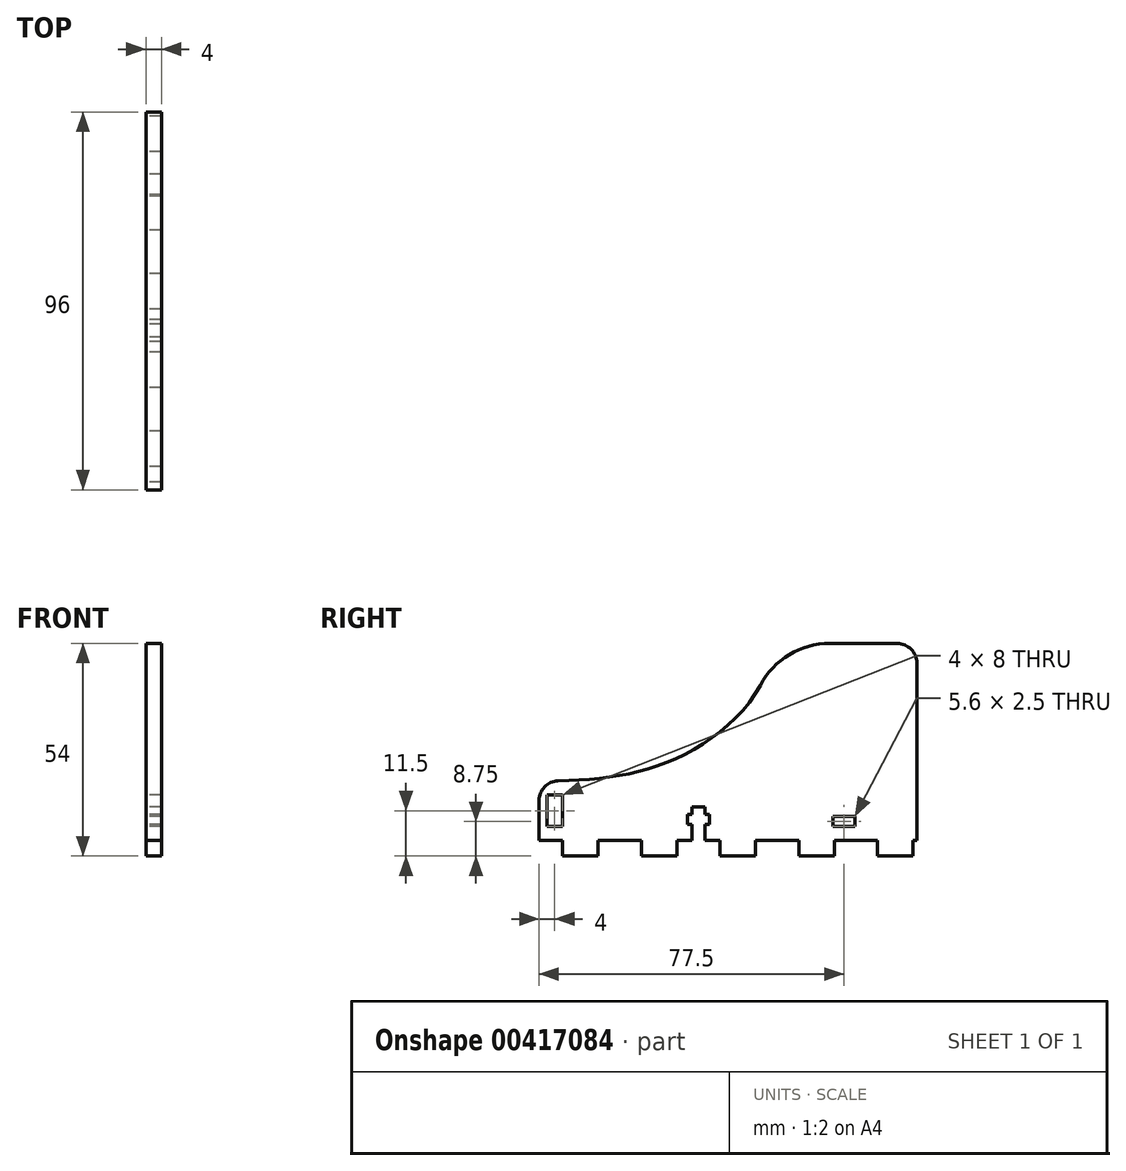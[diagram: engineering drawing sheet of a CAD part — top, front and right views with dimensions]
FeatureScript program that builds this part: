
annotation { "Feature Type Name" : "Feature", "Feature Type Description" : "" }
export const myFeature = defineFeature(function(context is Context, id is Id, definition is map)
    precondition{}
    {
        {
            var Q0;
            Q0=qCreatedBy(makeId("Right.planeOp"),FACE);
            var sketch = newSketch(context, id + "F0", { "sketchPlane" : qUnion([Q0])});
            skLineSegment(sketch, "E0", {"start": v(49, 0) * mm, "end": v(49, -4) * mm});
            skLineSegment(sketch, "E1", {"start": v(49, -4) * mm, "end": v(40, -4) * mm});
            skLineSegment(sketch, "E2", {"start": v(40, -4) * mm, "end": v(40, 0) * mm});
            skLineSegment(sketch, "E3", {"start": v(40, 0) * mm, "end": v(29, 0) * mm});
            skLineSegment(sketch, "E4.1.0.0", {"start": v(29, 0) * mm, "end": v(29, -4) * mm});
            skLineSegment(sketch, "E4.1.0.1", {"start": v(20, 0) * mm, "end": v(9, 0) * mm});
            skLineSegment(sketch, "E4.1.0.2", {"start": v(29, -4) * mm, "end": v(20, -4) * mm});
            skLineSegment(sketch, "E4.1.0.3", {"start": v(20, -4) * mm, "end": v(20, 0) * mm});
            skLineSegment(sketch, "E4.2.0.0", {"start": v(9, 0) * mm, "end": v(9, -4) * mm});
            skLineSegment(sketch, "E4.2.0.2", {"start": v(9, -4) * mm, "end": v(0, -4) * mm});
            skLineSegment(sketch, "E4.2.0.3", {"start": v(0, -4) * mm, "end": v(0, 0) * mm});
            skLineSegment(sketch, "E4.3.0.0", {"start": v(-11, 0) * mm, "end": v(-11, -4) * mm});
            skLineSegment(sketch, "E4.3.0.1", {"start": v(-20, 0) * mm, "end": v(-31, 0) * mm});
            skLineSegment(sketch, "E4.3.0.2", {"start": v(-11, -4) * mm, "end": v(-20, -4) * mm});
            skLineSegment(sketch, "E4.3.0.3", {"start": v(-20, -4) * mm, "end": v(-20, 0) * mm});
            skLineSegment(sketch, "E4.4.0.0", {"start": v(-31, 0) * mm, "end": v(-31, -4) * mm});
            skLineSegment(sketch, "E4.4.0.1", {"start": v(-40, 0) * mm, "end": v(-51, 0) * mm, "construction": true});
            skLineSegment(sketch, "E4.4.0.2", {"start": v(-31, -4) * mm, "end": v(-40, -4) * mm});
            skLineSegment(sketch, "E4.4.0.3", {"start": v(-40, -4) * mm, "end": v(-40, 0) * mm});
            skLineSegment(sketch, "E4.direction1", {"start": v(29, 0) * mm, "end": v(9, 0) * mm, "construction": true});
            skLineSegment(sketch, "E5", {"start": v(49, 0) * mm, "end": v(49, 50) * mm, "construction": true});
            skLineSegment(sketch, "E6", {"start": v(49, 50) * mm, "end": v(13, 50) * mm});
            skLineSegment(sketch, "E7", {"start": v(-40, 0) * mm, "end": v(-46, 0) * mm});
            skLineSegment(sketch, "E8", {"start": v(-46, 0) * mm, "end": v(-46, 15) * mm});
            skLineSegment(sketch, "E9.bottom", {"start": v(28.7, 3.5) * mm, "end": v(34.3, 3.5) * mm});
            skLineSegment(sketch, "E9.top", {"start": v(28.7, 6) * mm, "end": v(34.3, 6) * mm});
            skLineSegment(sketch, "E9.left", {"start": v(28.7, 3.5) * mm, "end": v(28.7, 6) * mm});
            skLineSegment(sketch, "E9.right", {"start": v(34.3, 3.5) * mm, "end": v(34.3, 6) * mm});
            skPoint(sketch, "E9.middle", {"position": v(31.5, 4.75) * mm});
            skLineSegment(sketch, "E10", {"start": v(49, 50) * mm, "end": v(50, 50) * mm});
            skLineSegment(sketch, "E11", {"start": v(50, 50) * mm, "end": v(50, 0) * mm});
            skLineSegment(sketch, "E12", {"start": v(50, 0) * mm, "end": v(49, 0) * mm});
            skFitSpline(sketch, "E13", {"points": [v(13, 50) * mm, v(-8.72, 21.95) * mm, v(-46, 15) * mm], "startDerivative": vector(0, -73.18) * mm, "endDerivative": vector(-82.46, -0.55) * mm});
            skLineSegment(sketch, "E14.bottom", {"start": v(-40, 3.5) * mm, "end": v(-44, 3.5) * mm});
            skLineSegment(sketch, "E14.top", {"start": v(-40, 11.5) * mm, "end": v(-44, 11.5) * mm});
            skLineSegment(sketch, "E14.left", {"start": v(-40, 3.5) * mm, "end": v(-40, 11.5) * mm});
            skLineSegment(sketch, "E14.right", {"start": v(-44, 3.5) * mm, "end": v(-44, 11.5) * mm});
            skPoint(sketch, "E14.middle", {"position": v(-42, 7.5) * mm});
            skPoint(sketch, "E14.middle.positionSnap0", {"position": v(-46, 7.5) * mm});
            skPoint(sketch, "E14.centerSnap0", {"position": v(-46, 7.5) * mm});
            skLineSegment(sketch, "E15", {"start": v(-3.85, 0) * mm, "end": v(0, 0) * mm});
            skLineSegment(sketch, "E16", {"start": v(-3.85, 0) * mm, "end": v(-3.85, 4) * mm});
            skLineSegment(sketch, "E17", {"start": v(-3.85, 4) * mm, "end": v(-2.7, 4) * mm});
            skLineSegment(sketch, "E18", {"start": v(-2.7, 4) * mm, "end": v(-2.7, 6.5) * mm});
            skLineSegment(sketch, "E19", {"start": v(-2.7, 6.5) * mm, "end": v(-3.85, 6.5) * mm});
            skLineSegment(sketch, "E20", {"start": v(-3.85, 6.5) * mm, "end": v(-3.85, 8.5) * mm});
            skLineSegment(sketch, "E21", {"start": v(-3.85, 8.5) * mm, "end": v(-5.5, 8.5) * mm});
            skLineSegment(sketch, "E22", {"start": v(-5.5, 8.5) * mm, "end": v(-5.5, 3.54) * mm, "construction": true});
            skLineSegment(sketch, "E23.MirrorCS", {"start": v(-11, 0) * mm, "end": v(-7.15, 0) * mm});
            skLineSegment(sketch, "E24.MirrorCS", {"start": v(-7.15, 8.5) * mm, "end": v(-5.5, 8.5) * mm});
            skLineSegment(sketch, "E25.MirrorCS", {"start": v(-7.15, 4) * mm, "end": v(-8.3, 4) * mm});
            skLineSegment(sketch, "E26.MirrorCS", {"start": v(-7.15, 0) * mm, "end": v(-7.15, 4) * mm});
            skLineSegment(sketch, "E27.MirrorCS", {"start": v(-8.3, 4) * mm, "end": v(-8.3, 6.5) * mm});
            skLineSegment(sketch, "E28.MirrorCS", {"start": v(-8.3, 6.5) * mm, "end": v(-7.15, 6.5) * mm});
            skLineSegment(sketch, "E29.MirrorCS", {"start": v(-7.15, 6.5) * mm, "end": v(-7.15, 8.5) * mm});
            skSolve(sketch);
        }
        {
            var Q0;
            Q0=makeQuery(id+"F0.imprint","IMPRINT",FACE,{"disambiguationData":[TD([[makeQuery(id+"F0.imprint","IMPRINT",EDGE,{"derivedFrom":sQuery(id+"F0.wireOp",EDGE,"E0")}),-1.0]])]});
            extrude(context, id + "F1", {"entities" : qUnion([Q0]), "depth" : 4 * mm});
        }
        {
            var Q0;
            Q0=makeQuery(id+"F1.opExtrude","SWEPT_EDGE",EDGE,{"disambiguationData":[OSD([sQuery(id+"F0.wireOp",EDGE,"E6"),sQuery(id+"F0.wireOp",EDGE,"E13")])]});
            fillet(context, id + "F2", {"entities" : qUnion([Q0]), "radius" : 20 * mm, "tangentPropagation" : true, "allowEdgeOverflow" : false});
        }
        {
            var Q0;
            Q0=makeQuery(id+"F1.opExtrude","SWEPT_EDGE",EDGE,{"disambiguationData":[OSD([sQuery(id+"F0.wireOp",EDGE,"E10"),sQuery(id+"F0.wireOp",EDGE,"E11")])]});
            var Q1;
            Q1=makeQuery(id+"F1.opExtrude","SWEPT_EDGE",EDGE,{"disambiguationData":[OSD([sQuery(id+"F0.wireOp",EDGE,"E8"),sQuery(id+"F0.wireOp",EDGE,"E13")])]});
            fillet(context, id + "F3", {"entities" : qUnion([Q0, Q1]), "radius" : 5 * mm, "tangentPropagation" : true, "allowEdgeOverflow" : false});
        }
    });
